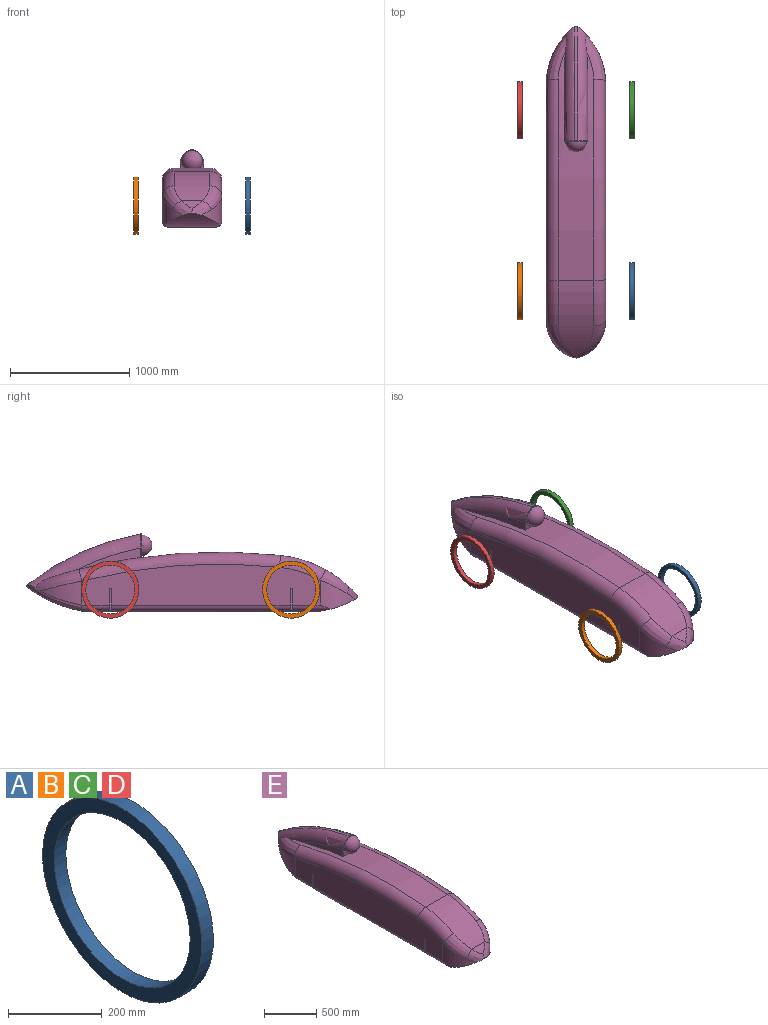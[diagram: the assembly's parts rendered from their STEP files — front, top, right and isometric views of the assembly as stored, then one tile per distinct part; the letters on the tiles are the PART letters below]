
ASSEMBLY  parts=5 mates=4
PART A: 4 faces, bbox 35x480x480 mm
  f0: cylinder r=205mm len=410mm, axis (-1,0,0), area 45081.9mm2, adj f2,f3
  f1: cylinder r=240mm len=480mm, axis (-1,0,0), area 52778.8mm2, adj f2,f3
  f2: plane 480x480mm, normal (1,0,0), area 48930.3mm2, adj f0,f1
  f3: plane 480x480mm, normal (-1,0,0), area 48930.3mm2, adj f0,f1
PART B: same geometry as A
PART C: same geometry as A
PART D: same geometry as A
PART E: 59 faces, bbox 504.2x2906.5x833.8 mm
  f0: cylinder r=635.32mm len=39.43mm, axis (0,0,-1), area 0mm2, adj f1,f58
  f1: torus R=2073.72mm, axis (1,0,0), area 137592.2mm2, adj f0,f2,f54,f55,f56,f57,f58
  f2: torus R=2140.81mm, axis (-1,0,0), area 30725.1mm2, adj f1,f3,f13,f53,f58
  f3: bspline ~37.91x9.62mm, area 245.3mm2, adj f2,f4,f12,f54
  f4: plane 49.31x6.22mm, normal (0,-1,0), area 83.2mm2, adj f3,f5,f12,f54
  f5: sphere r=90mm, area 50893.8mm2, adj f4,f6,f7,f11
  f6: plane 67.5x63.35mm, normal (0,1,0), area 203.1mm2, adj f5,f12
  f7: plane 190x119.12mm, normal (0,-1,0), area 6306.3mm2, adj f5,f8,f10,f12,f54,f56
  f8: cylinder r=5mm len=79.43mm, axis (0,0,1), area 621.2mm2, adj f7,f9,f12,f56
  f9: plane 549.44x188.07mm, normal (1,0,0), area 26697.7mm2, adj f8,f53,f56
  f10: cylinder r=5mm len=79.43mm, axis (0,0,1), area 621.2mm2, adj f7,f54,f55,f56
  f11: plane 67.5x63.35mm, normal (0,1,0), area 203.1mm2, adj f5,f54
  f12: bspline ~135.02x99.8mm, area 1279.6mm2, adj f3,f4,f6,f7,f8,f53
  f13: bspline ~519.26x277.62mm, area 37758.7mm2, adj f2,f14,f15,f41,f50,f51,f52,f53
  f14: cylinder r=635.32mm len=39.43mm, axis (0,0,-1), area 0mm2, adj f13,f53
  f15: cylinder r=1121.31mm len=439.29mm, axis (-1,0,0), area 127759.4mm2, adj f13,f16,f40,f41,f58
  f16: cylinder r=50mm len=2093.67mm, axis (0,-1,0), area 158282.1mm2, adj f15,f17,f19,f20,f22,f23,f24,f37
  f17: plane 183.3x20mm, normal (-1,0,0), area 3623.1mm2, adj f16,f18,f19,f39
  f18: cylinder r=10mm len=25mm, axis (-1,0,0), area 785.4mm2, adj f17,f19,f38,f39
  f19: plane 173.3x25mm, normal (0,1,0), area 4017.7mm2, adj f16,f17,f18,f38
  f20: plane 173.3x25mm, normal (0,-1,0), area 4017.7mm2, adj f16,f21,f22,f38
  f21: cylinder r=10mm len=25mm, axis (-1,0,0), area 785.4mm2, adj f20,f22,f23,f38
  f22: plane 183.3x20mm, normal (-1,0,0), area 3623.1mm2, adj f16,f20,f21,f23
  f23: plane 173.3x25mm, normal (0,1,0), area 4017.7mm2, adj f16,f21,f22,f38
  f24: cylinder r=336.25mm len=294.81mm, axis (0,0,-1), area 45388.1mm2, adj f16,f25,f36,f37,f38
  f25: bspline ~280.81x218.82mm, area 34763.1mm2, adj f24,f26,f33,f36
  f26: cylinder r=1000mm len=556.49mm, axis (-1,0,0), area 172125.6mm2, adj f25,f27,f29,f32,f33,f56
  f27: torus R=900mm, axis (1,0,0), area 60735.4mm2, adj f26,f28,f29,f50
  f28: torus R=4718.85mm, axis (1,0,0), area 265793.1mm2, adj f27,f50,f51,f52,f56
  f29: bspline ~280.81x218.82mm, area 34763.1mm2, adj f26,f27,f30,f31
  f30: cylinder r=336.25mm len=294.81mm, axis (0,0,-1), area 45388.1mm2, adj f29,f31,f37,f41,f50
  f31: bspline ~203.42x155.04mm, area 14435.1mm2, adj f29,f30,f32,f36,f37
  f32: cylinder r=1077.82mm len=176.97mm, axis (-1,0,0), area 8272.7mm2, adj f26,f31,f36
  f33: torus R=900mm, axis (-1,0,0), area 60735.4mm2, adj f25,f26,f34,f38
  f34: torus R=4718.85mm, axis (-1,0,0), area 265793.1mm2, adj f33,f35,f38,f56,f57
  f35: cylinder r=635.32mm len=349.48mm, axis (0,0,-1), area 41047.7mm2, adj f34,f38,f57,f58
  f36: bspline ~203.42x155.04mm, area 14435.1mm2, adj f24,f25,f31,f32,f37
  f37: cylinder r=700mm len=473.59mm, axis (-1,0,0), area 111955.3mm2, adj f16,f24,f30,f31,f36,f40,f41
  f38: plane 2000.02x344.53mm, normal (-1,0,0), area 600755.7mm2, adj f16,f18,f19,f20,f21,f23,f24,f33
  f39: plane 173.3x25mm, normal (0,-1,0), area 4017.7mm2, adj f16,f17,f18,f38
  f40: plane 2000x400mm, normal (0,0,-1), area 800000mm2, adj f15,f16,f37,f41
  f41: cylinder r=50mm len=2093.67mm, axis (0,-1,0), area 158282mm2, adj f13,f15,f30,f37,f40,f42,f44,f45
  f42: plane 173.3x25mm, normal (0,1,0), area 4017.7mm2, adj f41,f43,f44,f50
  f43: cylinder r=10mm len=25mm, axis (1,0,0), area 785.4mm2, adj f42,f44,f45,f50
  f44: plane 183.3x20mm, normal (1,0,0), area 3623.1mm2, adj f41,f42,f43,f45
  f45: plane 173.3x25mm, normal (0,-1,0), area 4017.7mm2, adj f41,f43,f44,f50
  f46: plane 173.3x25mm, normal (0,1,0), area 4017.7mm2, adj f41,f47,f48,f50
  f47: cylinder r=10mm len=25mm, axis (1,0,0), area 785.4mm2, adj f46,f48,f49,f50
  f48: plane 183.3x20mm, normal (1,0,0), area 3623.1mm2, adj f41,f46,f47,f49
  f49: plane 173.3x25mm, normal (0,-1,0), area 4017.7mm2, adj f41,f47,f48,f50
  f50: plane 2000.02x344.53mm, normal (1,0,0), area 600755.7mm2, adj f13,f27,f28,f30,f41,f42,f43,f45
  f51: cylinder r=635.32mm len=349.48mm, axis (0,0,-1), area 41047.5mm2, adj f13,f28,f50,f52
  f52: bspline ~453.56x245.65mm, area 54816.2mm2, adj f13,f28,f51,f53,f56
  f53: torus R=2073.72mm, axis (-1,0,0), area 137591.9mm2, adj f2,f9,f12,f13,f14,f52,f56
  f54: bspline ~135.02x99.8mm, area 1279.6mm2, adj f1,f3,f4,f7,f10,f11
  f55: plane 549.44x188.07mm, normal (-1,0,0), area 26697.7mm2, adj f1,f10,f56
  f56: cylinder r=4818.85mm len=1914.71mm, axis (-1,0,0), area 419958.7mm2, adj f1,f7,f8,f9,f10,f26,f28,f34
  f57: bspline ~453.56x245.65mm, area 54816.2mm2, adj f1,f34,f35,f56,f58
  f58: bspline ~519.26x277.62mm, area 37758.7mm2, adj f0,f1,f2,f13,f15,f16,f35,f38
PLACE A t=(337.34,-848.04,319.84)mm
PLACE B t=(-602.66,-848.04,319.84)mm
PLACE C t=(337.34,669.96,319.84)mm
PLACE D t=(-602.66,669.96,319.84)mm
PLACE E t=(-115.16,409.96,139.84)mm
MATE fastened B.f0 <-> E.f21  axis (1,0,0) through (-567.66,-848.04,319.84)mm
MATE fastened C.f0 <-> E.f18  axis (-1,0,0) through (337.34,669.96,319.84)mm
MATE fastened A.f0 <-> E.f21  axis (-1,0,0) through (337.34,-848.04,319.84)mm
MATE fastened D.f0 <-> E.f18  axis (1,0,0) through (-567.66,669.96,319.84)mm
